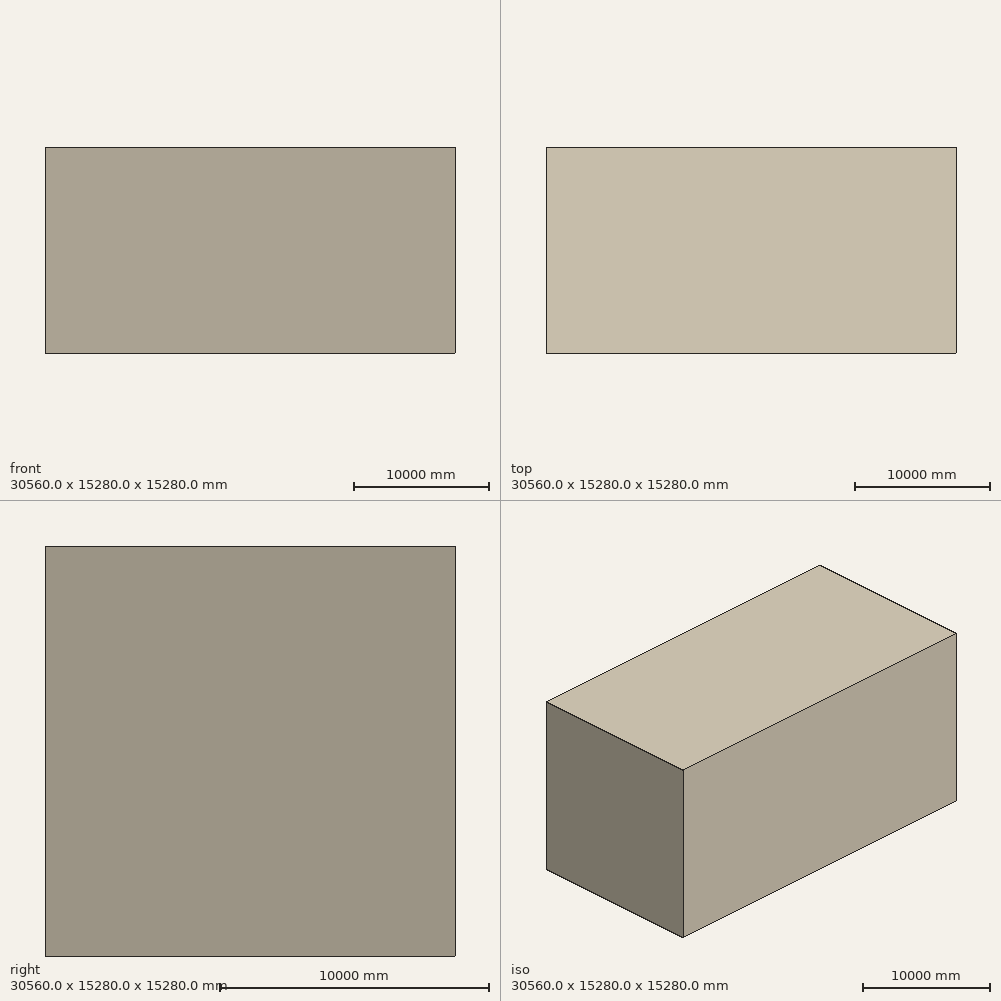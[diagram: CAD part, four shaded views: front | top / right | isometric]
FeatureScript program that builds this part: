
annotation { "Feature Type Name" : "Feature", "Feature Type Description" : "" }
export const myFeature = defineFeature(function(context is Context, id is Id, definition is map)
    precondition{}
    {
        {
            var Q0;
            Q0=qCreatedBy(makeId("Top.planeOp"),FACE);
            cPlane(context, id + "F0", {"entities" : qUnion([Q0]), "cplaneType" : CPlaneType.OFFSET, "offset" : 15140 * mm, "oppositeDirection" : true, "width" : 150 * mm, "height" : 150 * mm});
        }
        {
            var Q0;
            Q0=qCreatedBy(id+"F0.planeOp",FACE);
            var sketch = newSketch(context, id + "F1", { "sketchPlane" : qUnion([Q0])});
            skLineSegment(sketch, "E0.bottom", {"start": v(15280, -7640) * mm, "end": v(-15280, -7640) * mm});
            skLineSegment(sketch, "E0.top", {"start": v(15280, 7640) * mm, "end": v(-15280, 7640) * mm});
            skLineSegment(sketch, "E0.left", {"start": v(15280, -7640) * mm, "end": v(15280, 7640) * mm});
            skLineSegment(sketch, "E0.right", {"start": v(-15280, -7640) * mm, "end": v(-15280, 7640) * mm});
            skPoint(sketch, "E0.middle", {"position": v(0, 0) * mm});
            skSolve(sketch);
        }
        {
            var Q0;
            Q0=makeQuery(id+"F1.imprint","IMPRINT",FACE,{"disambiguationData":[TD([[makeQuery(id+"F1.imprint","IMPRINT",EDGE,{"derivedFrom":sQuery(id+"F1.wireOp",EDGE,"E0.bottom")}),-1.0]])]});
            extrude(context, id + "F2", {"entities" : qUnion([Q0]), "depth" : 140 * mm, "offsetDistance" : 25 * mm});
        }
        {
            var Q0;
            Q0=makeQuery(id+"F2.opExtrude","CAP_FACE",FACE,{"disambiguationData":[OSD([sQuery(id+"F1.wireOp",EDGE,"E0.bottom"),sQuery(id+"F1.wireOp",EDGE,"E0.top"),sQuery(id+"F1.wireOp",EDGE,"E0.left"),sQuery(id+"F1.wireOp",EDGE,"E0.right")])],"isStart":false});
            var sketch = newSketch(context, id + "F3", { "sketchPlane" : qUnion([Q0])});
            skPoint(sketch, "E1", {"position": v(-15280, 7640) * mm});
            skPoint(sketch, "E2", {"position": v(15280, 7640) * mm});
            skPoint(sketch, "E3", {"position": v(15280, -7640) * mm});
            skPoint(sketch, "E4", {"position": v(-15280, -7640) * mm});
            skPoint(sketch, "E5", {"position": v(-15280, -7500) * mm});
            skPoint(sketch, "E6", {"position": v(-15280, 7500) * mm});
            skPoint(sketch, "E7", {"position": v(-15140, 7640) * mm});
            skPoint(sketch, "E8", {"position": v(-15140, -7640) * mm});
            skPoint(sketch, "E9", {"position": v(15140, -7640) * mm});
            skPoint(sketch, "E10", {"position": v(15280, -7500) * mm});
            skPoint(sketch, "E11", {"position": v(15280, 7500) * mm});
            skPoint(sketch, "E12", {"position": v(15140, 7640) * mm});
            skPoint(sketch, "E13", {"position": v(140, 7640) * mm});
            skPoint(sketch, "E14", {"position": v(-140, 7640) * mm});
            skPoint(sketch, "E15", {"position": v(-140, -7640) * mm});
            skPoint(sketch, "E16", {"position": v(140, -7640) * mm});
            skPoint(sketch, "E17", {"position": v(-15140, 7500) * mm});
            skPoint(sketch, "E18", {"position": v(-15140, -7500) * mm});
            skPoint(sketch, "E19", {"position": v(15140, -7500) * mm});
            skPoint(sketch, "E20", {"position": v(15140, 7500) * mm});
            skLineSegment(sketch, "E21", {"start": v(-15280, -7640) * mm, "end": v(15280, -7640) * mm});
            skLineSegment(sketch, "E22", {"start": v(15280, -7640) * mm, "end": v(15280, 7640) * mm});
            skLineSegment(sketch, "E23", {"start": v(15280, 7640) * mm, "end": v(-15280, 7640) * mm});
            skLineSegment(sketch, "E24", {"start": v(-15280, 7640) * mm, "end": v(-15280, -7640) * mm});
            skPoint(sketch, "E25", {"position": v(-140, 7500) * mm});
            skPoint(sketch, "E26", {"position": v(140, 7500) * mm});
            skPoint(sketch, "E27", {"position": v(-140, -7500) * mm});
            skPoint(sketch, "E28", {"position": v(140, -7500) * mm});
            skLineSegment(sketch, "E29", {"start": v(-15140, 7500) * mm, "end": v(-140, 7500) * mm});
            skLineSegment(sketch, "E30", {"start": v(-140, 7500) * mm, "end": v(-140, -7500) * mm});
            skLineSegment(sketch, "E31", {"start": v(-140, -7500) * mm, "end": v(-15140, -7500) * mm});
            skLineSegment(sketch, "E32", {"start": v(-15140, -7500) * mm, "end": v(-15140, 7500) * mm});
            skLineSegment(sketch, "E33", {"start": v(140, 7500) * mm, "end": v(140, -7500) * mm});
            skLineSegment(sketch, "E34", {"start": v(140, -7500) * mm, "end": v(15140, -7500) * mm});
            skLineSegment(sketch, "E35", {"start": v(15140, -7500) * mm, "end": v(15140, 7500) * mm});
            skLineSegment(sketch, "E36", {"start": v(15140, 7500) * mm, "end": v(140, 7500) * mm});
            skSolve(sketch);
        }
        {
            var Q0;
            Q0=makeQuery(id+"F3.imprint","IMPRINT",FACE,{"disambiguationData":[TD([[makeQuery(id+"F3.imprint","IMPRINT",EDGE,{"derivedFrom":sQuery(id+"F3.wireOp",EDGE,"E21")}),-1.0]])]});
            extrude(context, id + "F4", {"entities" : qUnion([Q0]), "operationType" : NewBodyOperationType.ADD, "depth" : 6850 * mm, "offsetDistance" : 25 * mm});
        }
        {
            var Q0;
            Q0=makeQuery(id+"F4.opExtrude","CAP_FACE",FACE,{"disambiguationData":[OSD([sQuery(id+"F3.wireOp",EDGE,"E21"),sQuery(id+"F3.wireOp",EDGE,"E22"),sQuery(id+"F3.wireOp",EDGE,"E23"),sQuery(id+"F3.wireOp",EDGE,"E24"),sQuery(id+"F3.wireOp",EDGE,"E29"),sQuery(id+"F3.wireOp",EDGE,"E30"),sQuery(id+"F3.wireOp",EDGE,"E31"),sQuery(id+"F3.wireOp",EDGE,"E32"),sQuery(id+"F3.wireOp",EDGE,"E33"),sQuery(id+"F3.wireOp",EDGE,"E34"),sQuery(id+"F3.wireOp",EDGE,"E35"),sQuery(id+"F3.wireOp",EDGE,"E36")])],"isStart":false});
            var sketch = newSketch(context, id + "F5", { "sketchPlane" : qUnion([Q0])});
            skPoint(sketch, "E37", {"position": v(-15280, 7640) * mm});
            skPoint(sketch, "E38", {"position": v(-15280, -7640) * mm});
            skPoint(sketch, "E39", {"position": v(15280, -7640) * mm});
            skPoint(sketch, "E40", {"position": v(15280, 7640) * mm});
            skPoint(sketch, "E41", {"position": v(-15140, 7500) * mm});
            skPoint(sketch, "E42", {"position": v(-15140, -7500) * mm});
            skPoint(sketch, "E43", {"position": v(-140, -7500) * mm});
            skPoint(sketch, "E44", {"position": v(140, -7500) * mm});
            skPoint(sketch, "E45", {"position": v(15140, -7500) * mm});
            skPoint(sketch, "E46", {"position": v(-140, 7500) * mm});
            skPoint(sketch, "E47", {"position": v(140, 7500) * mm});
            skPoint(sketch, "E48", {"position": v(15140, 7500) * mm});
            skPoint(sketch, "E49", {"position": v(-140, 650) * mm});
            skPoint(sketch, "E50", {"position": v(140, 650) * mm});
            skPoint(sketch, "E51", {"position": v(-140, -650) * mm});
            skPoint(sketch, "E52", {"position": v(140, -650) * mm});
            skLineSegment(sketch, "E53", {"start": v(-15280, 7640) * mm, "end": v(15280, 7640) * mm});
            skLineSegment(sketch, "E54", {"start": v(15280, 7640) * mm, "end": v(15280, -7640) * mm});
            skLineSegment(sketch, "E55", {"start": v(15280, -7640) * mm, "end": v(-15280, -7640) * mm});
            skLineSegment(sketch, "E56", {"start": v(-15280, -7640) * mm, "end": v(-15280, 7640) * mm});
            skLineSegment(sketch, "E57", {"start": v(-15140, 7500) * mm, "end": v(-15140, -7500) * mm});
            skLineSegment(sketch, "E58", {"start": v(-15140, -7500) * mm, "end": v(-140, -7500) * mm});
            skLineSegment(sketch, "E59", {"start": v(-140, -7500) * mm, "end": v(-140, -650) * mm});
            skLineSegment(sketch, "E60", {"start": v(-140, -650) * mm, "end": v(140, -650) * mm});
            skLineSegment(sketch, "E61", {"start": v(140, -650) * mm, "end": v(140, -7500) * mm});
            skLineSegment(sketch, "E62", {"start": v(140, -7500) * mm, "end": v(15140, -7500) * mm});
            skLineSegment(sketch, "E63", {"start": v(15140, -7500) * mm, "end": v(15140, 7500) * mm});
            skLineSegment(sketch, "E64", {"start": v(15140, 7500) * mm, "end": v(140, 7500) * mm});
            skLineSegment(sketch, "E65", {"start": v(140, 7500) * mm, "end": v(140, 650) * mm});
            skLineSegment(sketch, "E66", {"start": v(140, 650) * mm, "end": v(-140, 650) * mm});
            skLineSegment(sketch, "E67", {"start": v(-140, 650) * mm, "end": v(-140, 7500) * mm});
            skLineSegment(sketch, "E68", {"start": v(-140, 7500) * mm, "end": v(-15140, 7500) * mm});
            skSolve(sketch);
        }
        {
            var Q0;
            Q0=makeQuery(id+"F5.imprint","IMPRINT",FACE,{"disambiguationData":[TD([[makeQuery(id+"F5.imprint","IMPRINT",EDGE,{"derivedFrom":sQuery(id+"F5.wireOp",EDGE,"E53")}),1.0]])]});
            extrude(context, id + "F6", {"entities" : qUnion([Q0]), "operationType" : NewBodyOperationType.ADD, "depth" : 1300 * mm, "offsetDistance" : 25 * mm});
        }
        {
            var Q0;
            Q0=makeQuery(id+"F6.opExtrude","CAP_FACE",FACE,{"disambiguationData":[OSD([sQuery(id+"F5.wireOp",EDGE,"E53"),sQuery(id+"F5.wireOp",EDGE,"E54"),sQuery(id+"F5.wireOp",EDGE,"E55"),sQuery(id+"F5.wireOp",EDGE,"E56"),sQuery(id+"F5.wireOp",EDGE,"E57"),sQuery(id+"F5.wireOp",EDGE,"E58"),sQuery(id+"F5.wireOp",EDGE,"E59"),sQuery(id+"F5.wireOp",EDGE,"E60"),sQuery(id+"F5.wireOp",EDGE,"E61"),sQuery(id+"F5.wireOp",EDGE,"E62"),sQuery(id+"F5.wireOp",EDGE,"E63"),sQuery(id+"F5.wireOp",EDGE,"E64"),sQuery(id+"F5.wireOp",EDGE,"E65"),sQuery(id+"F5.wireOp",EDGE,"E66"),sQuery(id+"F5.wireOp",EDGE,"E67"),sQuery(id+"F5.wireOp",EDGE,"E68")])],"isStart":false});
            var sketch = newSketch(context, id + "F7", { "sketchPlane" : qUnion([Q0])});
            skPoint(sketch, "E69", {"position": v(-15280, 7640) * mm});
            skPoint(sketch, "E70", {"position": v(15280, 7640) * mm});
            skPoint(sketch, "E71", {"position": v(15280, -7640) * mm});
            skPoint(sketch, "E72", {"position": v(-15280, -7640) * mm});
            skPoint(sketch, "E73", {"position": v(-15140, 7500) * mm});
            skPoint(sketch, "E74", {"position": v(-15140, -7500) * mm});
            skPoint(sketch, "E75", {"position": v(-140, -7500) * mm});
            skPoint(sketch, "E76", {"position": v(-140, 7500) * mm});
            skPoint(sketch, "E77", {"position": v(140, 7500) * mm});
            skPoint(sketch, "E78", {"position": v(140, -7500) * mm});
            skPoint(sketch, "E79", {"position": v(15140, -7500) * mm});
            skPoint(sketch, "E80", {"position": v(15140, 7500) * mm});
            skLineSegment(sketch, "E81", {"start": v(-15280, 7640) * mm, "end": v(15280, 7640) * mm});
            skLineSegment(sketch, "E82", {"start": v(15280, 7640) * mm, "end": v(15280, -7640) * mm});
            skLineSegment(sketch, "E83", {"start": v(15280, -7640) * mm, "end": v(-15280, -7640) * mm});
            skLineSegment(sketch, "E84", {"start": v(-15280, -7640) * mm, "end": v(-15280, 7640) * mm});
            skLineSegment(sketch, "E85", {"start": v(-15140, 7500) * mm, "end": v(-140, 7500) * mm});
            skLineSegment(sketch, "E86", {"start": v(-140, 7500) * mm, "end": v(-140, -7500) * mm});
            skLineSegment(sketch, "E87", {"start": v(-140, -7500) * mm, "end": v(-15140, -7500) * mm});
            skLineSegment(sketch, "E88", {"start": v(-15140, -7500) * mm, "end": v(-15140, 7500) * mm});
            skLineSegment(sketch, "E89", {"start": v(140, 7500) * mm, "end": v(15140, 7500) * mm});
            skLineSegment(sketch, "E90", {"start": v(15140, 7500) * mm, "end": v(15140, -7500) * mm});
            skLineSegment(sketch, "E91", {"start": v(15140, -7500) * mm, "end": v(140, -7500) * mm});
            skLineSegment(sketch, "E92", {"start": v(140, -7500) * mm, "end": v(140, 7500) * mm});
            skSolve(sketch);
        }
        {
            var Q0;
            Q0=makeQuery(id+"FslW42JygYK1mTL_1.boolean.opBoolean","MERGE",FACE,{"derivedFrom":[makeQuery(id+"F6.boolean.opBoolean","MERGE",FACE,{"derivedFrom":[makeQuery(id+"F4.boolean.opBoolean","MERGE",FACE,{"derivedFrom":[makeQuery(id+"F2.opExtrude","SWEPT_FACE",FACE,{"disambiguationData":[OSD([sQuery(id+"F1.wireOp",EDGE,"E0.right")])]}),makeQuery(id+"F4.opExtrude","SWEPT_FACE",FACE,{"disambiguationData":[OSD([sQuery(id+"F3.wireOp",EDGE,"E24")])]})]}),makeQuery(id+"F6.opExtrude","SWEPT_FACE",FACE,{"disambiguationData":[OSD([sQuery(id+"F5.wireOp",EDGE,"E56")])]})]}),makeQuery(id+"FslW42JygYK1mTL_1.opExtrude","SWEPT_FACE",FACE,{"disambiguationData":[OSD([sQuery(id+"F7.wireOp",EDGE,"E84")])]})]});
            cPlane(context, id + "F8", {"entities" : qUnion([Q0]), "cplaneType" : CPlaneType.OFFSET, "offset" : 15140 * mm, "oppositeDirection" : true, "width" : 150 * mm, "height" : 150 * mm});
        }
        {
            var Q0;
            Q0=qCreatedBy(id+"F8.planeOp",FACE);
            var sketch = newSketch(context, id + "F9", { "sketchPlane" : qUnion([Q0])});
            skPoint(sketch, "E93", {"position": v(0, -7500) * mm});
            skLineSegment(sketch, "E94.bottom", {"start": v(650, -6850) * mm, "end": v(-650, -6850) * mm});
            skLineSegment(sketch, "E94.top", {"start": v(650, -8150) * mm, "end": v(-650, -8150) * mm});
            skLineSegment(sketch, "E94.left", {"start": v(650, -6850) * mm, "end": v(650, -8150) * mm});
            skLineSegment(sketch, "E94.right", {"start": v(-650, -6850) * mm, "end": v(-650, -8150) * mm});
            skCircle(sketch, "E95", {"center": v(0, -7500) * mm, "radius": 650 * mm});
            skSolve(sketch);
        }
        {
            var Q0;
            Q0=makeQuery(id+"F6.opExtrude","CAP_FACE",FACE,{"disambiguationData":[OSD([sQuery(id+"F5.wireOp",EDGE,"E53"),sQuery(id+"F5.wireOp",EDGE,"E54"),sQuery(id+"F5.wireOp",EDGE,"E55"),sQuery(id+"F5.wireOp",EDGE,"E56"),sQuery(id+"F5.wireOp",EDGE,"E57"),sQuery(id+"F5.wireOp",EDGE,"E58"),sQuery(id+"F5.wireOp",EDGE,"E59"),sQuery(id+"F5.wireOp",EDGE,"E60"),sQuery(id+"F5.wireOp",EDGE,"E61"),sQuery(id+"F5.wireOp",EDGE,"E62"),sQuery(id+"F5.wireOp",EDGE,"E63"),sQuery(id+"F5.wireOp",EDGE,"E64"),sQuery(id+"F5.wireOp",EDGE,"E65"),sQuery(id+"F5.wireOp",EDGE,"E66"),sQuery(id+"F5.wireOp",EDGE,"E67"),sQuery(id+"F5.wireOp",EDGE,"E68")])],"isStart":false});
            var sketch = newSketch(context, id + "F10", { "sketchPlane" : qUnion([Q0])});
            skPoint(sketch, "E96", {"position": v(-15280, 7640) * mm});
            skPoint(sketch, "E97", {"position": v(-15280, -7640) * mm});
            skPoint(sketch, "E98", {"position": v(15280, -7640) * mm});
            skPoint(sketch, "E99", {"position": v(15280, 7640) * mm});
            skPoint(sketch, "E100", {"position": v(-15140, 7500) * mm});
            skPoint(sketch, "E101", {"position": v(-140, 7500) * mm});
            skPoint(sketch, "E102", {"position": v(-140, -7500) * mm});
            skPoint(sketch, "E103", {"position": v(-15140, -7500) * mm});
            skPoint(sketch, "E104", {"position": v(140, 7500) * mm});
            skPoint(sketch, "E105", {"position": v(15140, 7500) * mm});
            skPoint(sketch, "E106", {"position": v(15140, -7500) * mm});
            skPoint(sketch, "E107", {"position": v(140, -7500) * mm});
            skLineSegment(sketch, "E108", {"start": v(-15280, 7640) * mm, "end": v(-15280, -7640) * mm});
            skLineSegment(sketch, "E109", {"start": v(-15280, -7640) * mm, "end": v(15280, -7640) * mm});
            skLineSegment(sketch, "E110", {"start": v(15280, -7640) * mm, "end": v(15280, 7640) * mm});
            skLineSegment(sketch, "E111", {"start": v(15280, 7640) * mm, "end": v(-15280, 7640) * mm});
            skLineSegment(sketch, "E112", {"start": v(-15140, 7500) * mm, "end": v(-15140, -7500) * mm});
            skLineSegment(sketch, "E113", {"start": v(-15140, -7500) * mm, "end": v(-140, -7500) * mm});
            skLineSegment(sketch, "E114", {"start": v(-140, -7500) * mm, "end": v(-140, 7500) * mm});
            skLineSegment(sketch, "E115", {"start": v(140, 7500) * mm, "end": v(15140, 7500) * mm});
            skLineSegment(sketch, "E116", {"start": v(15140, 7500) * mm, "end": v(15140, -7500) * mm});
            skLineSegment(sketch, "E117", {"start": v(15140, -7500) * mm, "end": v(140, -7500) * mm});
            skLineSegment(sketch, "E118", {"start": v(140, -7500) * mm, "end": v(140, 7500) * mm});
            skSolve(sketch);
        }
        {
            var Q0;
            Q0=makeQuery(id+"F10.imprint","IMPRINT",FACE,{"disambiguationData":[TD([[makeQuery(id+"F10.imprint","IMPRINT",EDGE,{"derivedFrom":sQuery(id+"F10.wireOp",EDGE,"E108")}),-1.0]])]});
            var Q1;
            {var subQ1=makeQuery(id+"F6.opExtrude","CAP_EDGE",EDGE,{"disambiguationData":[OSD([sQuery(id+"F5.wireOp",EDGE,"E60")])],"isStart":false});Q1=makeQuery(id+"F10.imprint","IMPRINT",FACE,{"disambiguationData":[TD([[makeQuery(id+"F10.imprint","IMPRINT",EDGE,{"derivedFrom":subQ1}),1.0]])]});}
            extrude(context, id + "F11", {"entities" : qUnion([Q0, Q1]), "operationType" : NewBodyOperationType.ADD, "depth" : 6850 * mm, "offsetDistance" : 25 * mm});
        }
        {
            var Q0;
            {var subQ0=sQuery(id+"F9.wireOp",EDGE,"E94.left");var subQ1=sQuery(id+"F9.wireOp",EDGE,"E94.bottom");var subQ2=makeQuery(id+"F9.imprint","INTERSECT",VERTEX,{"derivedFrom":[subQ1,subQ0]});Q0=makeQuery(id+"F9.imprint","IMPRINT",FACE,{"disambiguationData":[TD([[makeQuery(id+"F9.imprint","IMPRINT",EDGE,{"disambiguationData":[TD([[subQ2,-1.0]])],"derivedFrom":subQ1}),1.0]])]});}
            var Q1;
            {var subQ0=sQuery(id+"F9.wireOp",EDGE,"E94.right");var subQ1=sQuery(id+"F9.wireOp",EDGE,"E94.bottom");var subQ2=makeQuery(id+"F9.imprint","INTERSECT",VERTEX,{"derivedFrom":[subQ1,subQ0]});Q1=makeQuery(id+"F9.imprint","IMPRINT",FACE,{"disambiguationData":[TD([[makeQuery(id+"F9.imprint","IMPRINT",EDGE,{"disambiguationData":[TD([[subQ2,1.0]])],"derivedFrom":subQ1}),1.0]])]});}
            var Q2;
            {var subQ0=sQuery(id+"F9.wireOp",EDGE,"E94.left");var subQ1=sQuery(id+"F9.wireOp",EDGE,"E94.top");var subQ2=makeQuery(id+"F9.imprint","INTERSECT",VERTEX,{"derivedFrom":[subQ1,subQ0]});Q2=makeQuery(id+"F9.imprint","IMPRINT",FACE,{"disambiguationData":[TD([[makeQuery(id+"F9.imprint","IMPRINT",EDGE,{"disambiguationData":[TD([[subQ2,-1.0]])],"derivedFrom":subQ1}),-1.0]])]});}
            var Q3;
            {var subQ0=sQuery(id+"F9.wireOp",EDGE,"E94.right");var subQ1=sQuery(id+"F9.wireOp",EDGE,"E94.top");var subQ2=makeQuery(id+"F9.imprint","INTERSECT",VERTEX,{"derivedFrom":[subQ1,subQ0]});Q3=makeQuery(id+"F9.imprint","IMPRINT",FACE,{"disambiguationData":[TD([[makeQuery(id+"F9.imprint","IMPRINT",EDGE,{"disambiguationData":[TD([[subQ2,1.0]])],"derivedFrom":subQ1}),-1.0]])]});}
            extrude(context, id + "F12", {"entities" : qUnion([Q0, Q1, Q2, Q3]), "operationType" : NewBodyOperationType.ADD, "oppositeDirection" : true, "depth" : 280 * mm, "offsetDistance" : 25 * mm});
        }
        {
            var Q0;
            Q0=makeQuery(id+"F11.opExtrude","CAP_FACE",FACE,{"disambiguationData":[OSD([sQuery(id+"F5.wireOp",EDGE,"E68"),sQuery(id+"F10.wireOp",EDGE,"E108"),sQuery(id+"F10.wireOp",EDGE,"E109"),sQuery(id+"F10.wireOp",EDGE,"E110"),sQuery(id+"F10.wireOp",EDGE,"E111"),sQuery(id+"F10.wireOp",EDGE,"E112"),sQuery(id+"F10.wireOp",EDGE,"E113"),sQuery(id+"F10.wireOp",EDGE,"E114"),sQuery(id+"F10.wireOp",EDGE,"E115"),sQuery(id+"F10.wireOp",EDGE,"E116"),sQuery(id+"F10.wireOp",EDGE,"E117"),sQuery(id+"F10.wireOp",EDGE,"E118")])],"isStart":false});
            var sketch = newSketch(context, id + "F13", { "sketchPlane" : qUnion([Q0])});
            skPoint(sketch, "E119", {"position": v(-15280, 7640) * mm});
            skPoint(sketch, "E120", {"position": v(15280, 7640) * mm});
            skPoint(sketch, "E121", {"position": v(-15280, -7640) * mm});
            skPoint(sketch, "E122", {"position": v(15280, -7640) * mm});
            skLineSegment(sketch, "E123", {"start": v(-15280, 7640) * mm, "end": v(15280, 7640) * mm});
            skLineSegment(sketch, "E124", {"start": v(15280, 7640) * mm, "end": v(15280, -7640) * mm});
            skLineSegment(sketch, "E125", {"start": v(15280, -7640) * mm, "end": v(-15280, -7640) * mm});
            skLineSegment(sketch, "E126", {"start": v(-15280, -7640) * mm, "end": v(-15280, 7640) * mm});
            skSolve(sketch);
        }
        {
            var Q0;
            Q0=makeQuery(id+"F13.imprint","IMPRINT",FACE,{"disambiguationData":[TD([[makeQuery(id+"F13.imprint","IMPRINT",EDGE,{"derivedFrom":sQuery(id+"F13.wireOp",EDGE,"E123")}),1.0]])]});
            var Q1;
            Q1=makeQuery(id+"F13.imprint","IMPRINT",FACE,{"disambiguationData":[TD([[makeQuery(id+"F13.imprint","IMPRINT",EDGE,{"derivedFrom":makeQuery(id+"F11.opExtrude","CAP_EDGE",EDGE,{"disambiguationData":[OSD([sQuery(id+"F10.wireOp",EDGE,"E112")])],"isStart":false})}),-1.0]])]});
            var Q2;
            Q2=makeQuery(id+"F13.imprint","IMPRINT",FACE,{"disambiguationData":[TD([[makeQuery(id+"F13.imprint","IMPRINT",EDGE,{"derivedFrom":makeQuery(id+"F11.opExtrude","CAP_EDGE",EDGE,{"disambiguationData":[OSD([sQuery(id+"F10.wireOp",EDGE,"E115")])],"isStart":false})}),1.0]])]});
            extrude(context, id + "F14", {"entities" : qUnion([Q0, Q1, Q2]), "operationType" : NewBodyOperationType.ADD, "depth" : 140 * mm, "offsetDistance" : 25 * mm});
        }
    });
